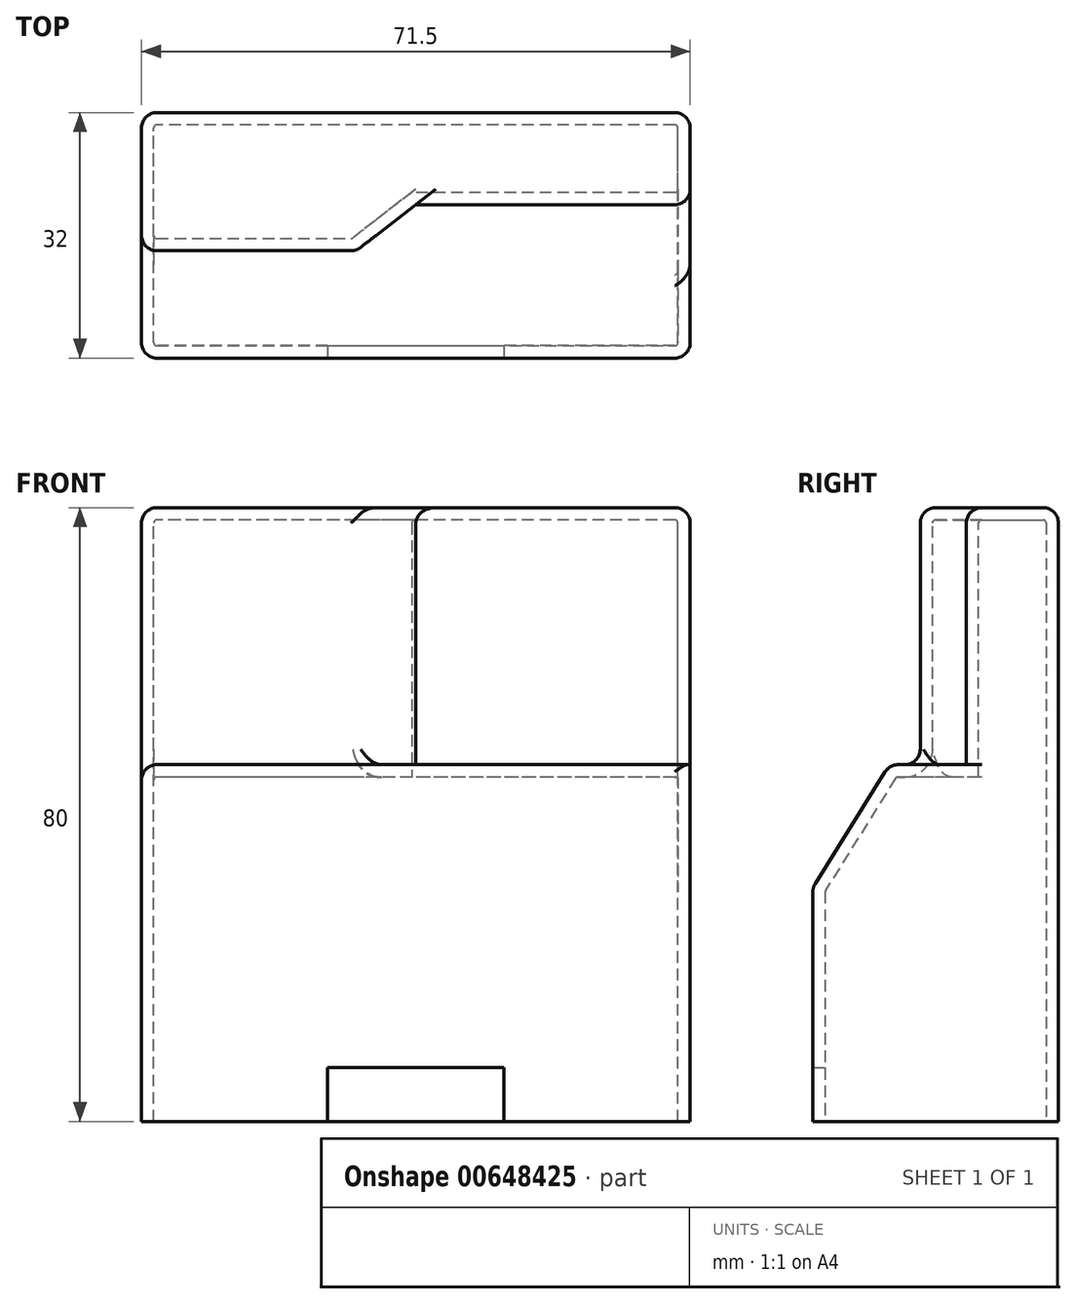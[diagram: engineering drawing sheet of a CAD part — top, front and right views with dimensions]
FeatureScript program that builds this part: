
annotation { "Feature Type Name" : "Feature", "Feature Type Description" : "" }
export const myFeature = defineFeature(function(context is Context, id is Id, definition is map)
    precondition{}
    {
        {
            var Q0;
            Q0=qCreatedBy(makeId("Top.planeOp"),FACE);
            var sketch = newSketch(context, id + "F0", { "sketchPlane" : qUnion([Q0])});
            skLineSegment(sketch, "E0.bottom", {"start": v(35.75, -16) * mm, "end": v(-35.75, -16) * mm});
            skLineSegment(sketch, "E0.top", {"start": v(35.75, 16) * mm, "end": v(-35.75, 16) * mm});
            skLineSegment(sketch, "E0.left", {"start": v(35.75, -16) * mm, "end": v(35.75, 16) * mm});
            skLineSegment(sketch, "E0.right", {"start": v(-35.75, -16) * mm, "end": v(-35.75, 16) * mm});
            skPoint(sketch, "E0.middle", {"position": v(0, 0) * mm});
            skSolve(sketch);
        }
        {
            var Q0;
            Q0 = qSketchRegion(id + "F0", true);
            extrude(context, id + "F1", {"entities" : qUnion([Q0]), "depth" : 30.5 * mm, "offsetDistance" : 25 * mm});
        }
        {
            var Q0;
            Q0=qCreatedBy(makeId("Right.planeOp"),FACE);
            var sketch = newSketch(context, id + "F2", { "sketchPlane" : qUnion([Q0])});
            skLineSegment(sketch, "E1", {"start": v(0, 0) * mm, "end": v(0, 30.5) * mm});
            skLineSegment(sketch, "E2", {"start": v(0, 30.5) * mm, "end": v(16, 30.5) * mm});
            skLineSegment(sketch, "E3", {"start": v(16, 30.5) * mm, "end": v(16, 46.5) * mm});
            skLineSegment(sketch, "E4", {"start": v(16, 46.5) * mm, "end": v(-6, 46.5) * mm});
            skLineSegment(sketch, "E5", {"start": v(0, 30.5) * mm, "end": v(-16, 30.5) * mm});
            skLineSegment(sketch, "E6", {"start": v(-16, 30.5) * mm, "end": v(-6, 46.5) * mm});
            skSolve(sketch);
        }
        {
            var Q0;
            Q0 = qSketchRegion(id + "F2", true);
            extrude(context, id + "F3", {"entities" : qUnion([Q0]), "operationType" : NewBodyOperationType.ADD, "endBound" : BoundingType.SYMMETRIC, "depth" : 71.5 * mm, "offsetDistance" : 25 * mm});
        }
        {
            var Q0;
            Q0=qCreatedBy(makeId("Right.planeOp"),FACE);
            var sketch = newSketch(context, id + "F4", { "sketchPlane" : qUnion([Q0])});
            skLineSegment(sketch, "E7", {"start": v(0, 0) * mm, "end": v(16, 0) * mm});
            skLineSegment(sketch, "E8", {"start": v(16, 0) * mm, "end": v(16, 46.5) * mm});
            skLineSegment(sketch, "E9", {"start": v(16, 46.5) * mm, "end": v(16, 80) * mm});
            skLineSegment(sketch, "E10", {"start": v(16, 80) * mm, "end": v(4, 80) * mm});
            skLineSegment(sketch, "E11", {"start": v(4, 80) * mm, "end": v(4, 46.5) * mm});
            skLineSegment(sketch, "E12", {"start": v(4, 46.5) * mm, "end": v(16, 46.5) * mm});
            skSolve(sketch);
        }
        {
            var Q0;
            Q0 = qSketchRegion(id + "F4", true);
            extrude(context, id + "F5", {"entities" : qUnion([Q0]), "operationType" : NewBodyOperationType.ADD, "endBound" : BoundingType.SYMMETRIC, "depth" : 71.5 * mm, "offsetDistance" : 25 * mm});
        }
        {
            var Q0;
            Q0=qCreatedBy(makeId("Top.planeOp"),FACE);
            var sketch = newSketch(context, id + "F6", { "sketchPlane" : qUnion([Q0])});
            skLineSegment(sketch, "E13", {"start": v(0, 0) * mm, "end": v(0, 16) * mm});
            skLineSegment(sketch, "E14", {"start": v(0, 16) * mm, "end": v(-35.75, 16) * mm});
            skLineSegment(sketch, "E15", {"start": v(-35.75, 16) * mm, "end": v(-35.75, -2) * mm});
            skLineSegment(sketch, "E16", {"start": v(-35.75, -2) * mm, "end": v(-7.75, -2) * mm});
            skLineSegment(sketch, "E17", {"start": v(0, 0) * mm, "end": v(0, 4) * mm});
            skLineSegment(sketch, "E18", {"start": v(0, 4) * mm, "end": v(-7.75, -2) * mm});
            skSolve(sketch);
        }
        {
            var Q0;
            Q0 = qSketchRegion(id + "F6", true);
            extrude(context, id + "F7", {"entities" : qUnion([Q0]), "operationType" : NewBodyOperationType.ADD, "depth" : 80 * mm, "offsetDistance" : 25 * mm});
        }
        {
            var Q0;
            Q0=makeQuery(id+"F7.opExtrude","SWEPT_EDGE",EDGE,{"disambiguationData":[OSD([sQuery(id+"F6.wireOp",EDGE,"E13"),sQuery(id+"F6.wireOp",EDGE,"E18")])]});
            var Q1;
            Q1=makeQuery(id+"F7.opExtrude","SWEPT_EDGE",EDGE,{"disambiguationData":[OSD([sQuery(id+"F6.wireOp",EDGE,"E16"),sQuery(id+"F6.wireOp",EDGE,"E18")])]});
            var Q2;
            Q2=makeQuery(id+"F5.opExtrude","SWEPT_EDGE",EDGE,{"disambiguationData":[OSD([sQuery(id+"F4.wireOp",EDGE,"E11"),sQuery(id+"F4.wireOp",EDGE,"E12")])]});
            var Q3;
            Q3=makeQuery(id+"F3.opExtrude","SWEPT_EDGE",EDGE,{"disambiguationData":[OSD([sQuery(id+"F2.wireOp",EDGE,"E4"),sQuery(id+"F2.wireOp",EDGE,"E6")])]});
            var Q4;
            Q4=makeQuery(id+"F3.boolean.opBoolean","MERGE",EDGE,{"derivedFrom":[makeQuery(id+"F1.opExtrude","CAP_EDGE",EDGE,{"disambiguationData":[OSD([sQuery(id+"F0.wireOp",EDGE,"E0.bottom")])],"isStart":false}),makeQuery(id+"F3.opExtrude","SWEPT_EDGE",EDGE,{"disambiguationData":[OSD([sQuery(id+"F2.wireOp",EDGE,"E5"),sQuery(id+"F2.wireOp",EDGE,"E6")])]})]});
            var Q5;
            Q5=makeQuery(id+"F5.opExtrude","CAP_EDGE",EDGE,{"disambiguationData":[OSD([sQuery(id+"F4.wireOp",EDGE,"E11")])],"isStart":false});
            var Q6;
            Q6=makeQuery(id+"F5.boolean.opBoolean","MERGE",EDGE,{"derivedFrom":[makeQuery(id+"F3.boolean.opBoolean","MERGE",EDGE,{"derivedFrom":[makeQuery(id+"F1.opExtrude","SWEPT_EDGE",EDGE,{"disambiguationData":[OSD([sQuery(id+"F0.wireOp",EDGE,"E0.top"),sQuery(id+"F0.wireOp",EDGE,"E0.left")])]}),makeQuery(id+"F3.opExtrude","CAP_EDGE",EDGE,{"disambiguationData":[OSD([sQuery(id+"F2.wireOp",EDGE,"E3")])],"isStart":false})]}),makeQuery(id+"F5.opExtrude","CAP_EDGE",EDGE,{"disambiguationData":[OSD([sQuery(id+"F4.wireOp",EDGE,"E9")])],"isStart":false})]});
            var Q7;
            Q7=makeQuery(id+"F5.opExtrude","SWEPT_EDGE",EDGE,{"disambiguationData":[OSD([sQuery(id+"F4.wireOp",EDGE,"E9"),sQuery(id+"F4.wireOp",EDGE,"E10")])]});
            var Q8;
            Q8=makeQuery(id+"F5.opExtrude","CAP_EDGE",EDGE,{"disambiguationData":[OSD([sQuery(id+"F4.wireOp",EDGE,"E10")])],"isStart":false});
            var Q9;
            Q9=makeQuery(id+"F5.opExtrude","SWEPT_EDGE",EDGE,{"disambiguationData":[OSD([sQuery(id+"F4.wireOp",EDGE,"E10"),sQuery(id+"F4.wireOp",EDGE,"E11")])]});
            var Q10;
            Q10=makeQuery(id+"F7.opExtrude","CAP_EDGE",EDGE,{"disambiguationData":[OSD([sQuery(id+"F6.wireOp",EDGE,"E16")])],"isStart":false});
            var Q11;
            Q11=makeQuery(id+"F7.boolean.opBoolean","MERGE",EDGE,{"derivedFrom":[makeQuery(id+"F5.opExtrude","CAP_EDGE",EDGE,{"disambiguationData":[OSD([sQuery(id+"F4.wireOp",EDGE,"E10")])],"isStart":true}),makeQuery(id+"F7.opExtrude","CAP_EDGE",EDGE,{"disambiguationData":[OSD([sQuery(id+"F6.wireOp",EDGE,"E15")])],"isStart":false})]});
            var Q12;
            Q12=makeQuery(id+"F7.opExtrude","SWEPT_EDGE",EDGE,{"disambiguationData":[OSD([sQuery(id+"F6.wireOp",EDGE,"E15"),sQuery(id+"F6.wireOp",EDGE,"E16")])]});
            var Q13;
            Q13=makeQuery(id+"F5.boolean.opBoolean","MERGE",EDGE,{"derivedFrom":[makeQuery(id+"F3.boolean.opBoolean","MERGE",EDGE,{"derivedFrom":[makeQuery(id+"F1.opExtrude","SWEPT_EDGE",EDGE,{"disambiguationData":[OSD([sQuery(id+"F0.wireOp",EDGE,"E0.top"),sQuery(id+"F0.wireOp",EDGE,"E0.right")])]}),makeQuery(id+"F3.opExtrude","CAP_EDGE",EDGE,{"disambiguationData":[OSD([sQuery(id+"F2.wireOp",EDGE,"E3")])],"isStart":true})]}),makeQuery(id+"F5.opExtrude","CAP_EDGE",EDGE,{"disambiguationData":[OSD([sQuery(id+"F4.wireOp",EDGE,"E9")])],"isStart":true})]});
            var Q14;
            Q14=makeQuery(id+"F3.opExtrude","CAP_EDGE",EDGE,{"disambiguationData":[OSD([sQuery(id+"F2.wireOp",EDGE,"E6")])],"isStart":true});
            var Q15;
            Q15=makeQuery(id+"F1.opExtrude","SWEPT_EDGE",EDGE,{"disambiguationData":[OSD([sQuery(id+"F0.wireOp",EDGE,"E0.bottom"),sQuery(id+"F0.wireOp",EDGE,"E0.right")])]});
            var Q16;
            Q16=makeQuery(id+"F3.opExtrude","CAP_EDGE",EDGE,{"disambiguationData":[OSD([sQuery(id+"F2.wireOp",EDGE,"E4")])],"isStart":true});
            var Q17;
            Q17=makeQuery(id+"F3.opExtrude","CAP_EDGE",EDGE,{"disambiguationData":[OSD([sQuery(id+"F2.wireOp",EDGE,"E6")])],"isStart":false});
            var Q18;
            Q18=makeQuery(id+"F1.opExtrude","SWEPT_EDGE",EDGE,{"disambiguationData":[OSD([sQuery(id+"F0.wireOp",EDGE,"E0.bottom"),sQuery(id+"F0.wireOp",EDGE,"E0.left")])]});
            var Q19;
            Q19=makeQuery(id+"F7.boolean.opBoolean","INTERSECT",EDGE,{"derivedFrom":[makeQuery(id+"F3.opExtrude","SWEPT_FACE",FACE,{"disambiguationData":[OSD([sQuery(id+"F2.wireOp",EDGE,"E4")])]}),makeQuery(id+"F7.opExtrude","SWEPT_FACE",FACE,{"disambiguationData":[OSD([sQuery(id+"F6.wireOp",EDGE,"E16")])]})]});
            fillet(context, id + "F8", {"entities" : qUnion([Q0, Q1, Q2, Q3, Q4, Q5, Q6, Q7, Q8, Q9, Q10, Q11, Q12, Q13, Q14, Q15, Q16, Q17, Q18, Q19]), "radius" : 2 * mm, "tangentPropagation" : true, "allowEdgeOverflow" : false});
        }
        {
            var Q0;
            Q0=makeQuery(id+"F1.opExtrude","CAP_FACE",FACE,{"disambiguationData":[OSD([sQuery(id+"F0.wireOp",EDGE,"E0.bottom"),sQuery(id+"F0.wireOp",EDGE,"E0.top"),sQuery(id+"F0.wireOp",EDGE,"E0.left"),sQuery(id+"F0.wireOp",EDGE,"E0.right")])],"isStart":true});
            shell(context, id + "F9", {"entities" : qUnion([Q0]), "thickness" : 1.6 * mm});
        }
        {
            var Q0;
            Q0=qCreatedBy(makeId("Front.planeOp"),FACE);
            var sketch = newSketch(context, id + "F10", { "sketchPlane" : qUnion([Q0])});
            skLineSegment(sketch, "E19.bottom", {"start": v(11.5, -7) * mm, "end": v(-11.5, -7) * mm});
            skLineSegment(sketch, "E19.top", {"start": v(11.5, 7) * mm, "end": v(-11.5, 7) * mm});
            skLineSegment(sketch, "E19.left", {"start": v(11.5, -7) * mm, "end": v(11.5, 7) * mm});
            skLineSegment(sketch, "E19.right", {"start": v(-11.5, -7) * mm, "end": v(-11.5, 7) * mm});
            skPoint(sketch, "E19.middle", {"position": v(0, 0) * mm});
            skSolve(sketch);
        }
        {
            var Q0;
            Q0 = qSketchRegion(id + "F10", true);
            extrude(context, id + "F11", {"entities" : qUnion([Q0]), "depth" : 25 * mm, "offsetDistance" : 25 * mm});
        }
        {
            var Q0;
            Q0=makeQuery(id+"F11.opExtrude","SWEPT_BODY",BODY,{"disambiguationData":[OSD([sQuery(id+"F10.wireOp",EDGE,"E19.bottom"),sQuery(id+"F10.wireOp",EDGE,"E19.top"),sQuery(id+"F10.wireOp",EDGE,"E19.left"),sQuery(id+"F10.wireOp",EDGE,"E19.right")])]});
            var Q1;
            Q1=makeQuery(id+"F1.opExtrude","SWEPT_BODY",BODY,{"disambiguationData":[OSD([sQuery(id+"F0.wireOp",EDGE,"E0.bottom"),sQuery(id+"F0.wireOp",EDGE,"E0.top"),sQuery(id+"F0.wireOp",EDGE,"E0.left"),sQuery(id+"F0.wireOp",EDGE,"E0.right")])]});
            booleanBodies(context, id + "F12", {"operationType" : BooleanOperationType.SUBTRACTION, "tools" : qUnion([Q0]), "targets" : qUnion([Q1])});
        }
    });
